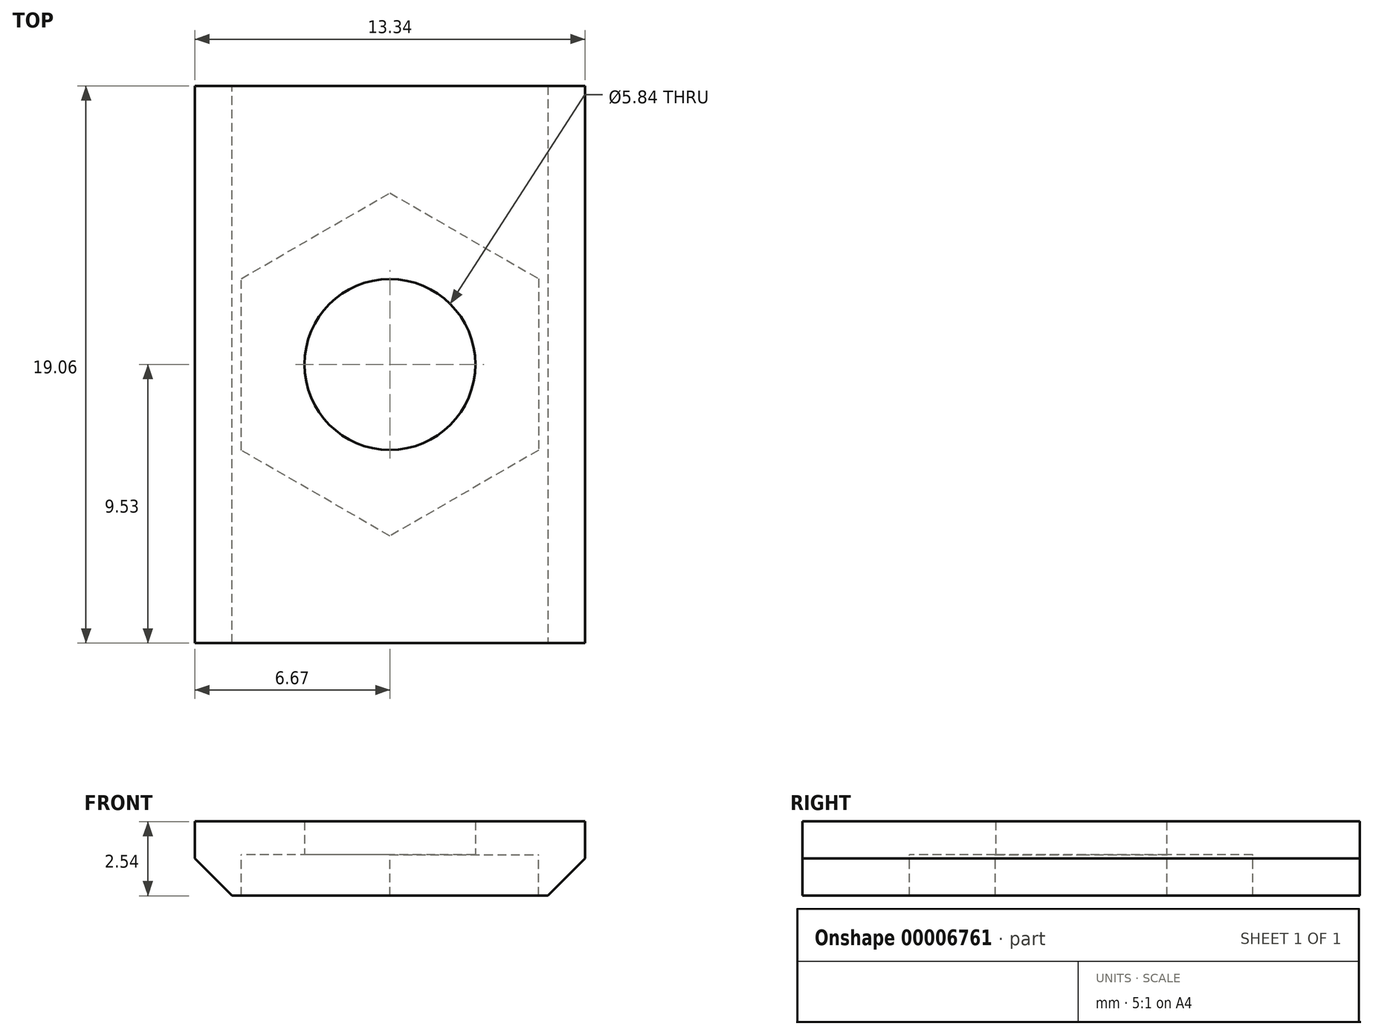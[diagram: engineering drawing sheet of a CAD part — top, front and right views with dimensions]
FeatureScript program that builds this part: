
annotation { "Feature Type Name" : "Feature", "Feature Type Description" : "" }
export const myFeature = defineFeature(function(context is Context, id is Id, definition is map)
    precondition{}
    {
        {
            var Q0;
            Q0=qCreatedBy(makeId("Top.planeOp"),FACE);
            var sketch = newSketch(context, id + "F0", { "sketchPlane" : qUnion([Q0])});
            skLineSegment(sketch, "E0.bottom", {"start": v(6.67, -9.53) * mm, "end": v(-6.67, -9.53) * mm});
            skLineSegment(sketch, "E0.top", {"start": v(6.67, 9.53) * mm, "end": v(-6.67, 9.53) * mm});
            skLineSegment(sketch, "E0.left", {"start": v(6.67, -9.53) * mm, "end": v(6.67, 9.53) * mm});
            skLineSegment(sketch, "E0.right", {"start": v(-6.67, -9.53) * mm, "end": v(-6.67, 9.53) * mm});
            skPoint(sketch, "E0.middle", {"position": v(0, 0) * mm});
            skCircle(sketch, "E1.cCircle", {"center": v(0, 0) * mm, "radius": 5.08 * mm, "construction": true});
            skLineSegment(sketch, "E1.0", {"start": v(5.08, -2.93) * mm, "end": v(0, -5.87) * mm});
            skLineSegment(sketch, "E1.1", {"start": v(0, -5.87) * mm, "end": v(-5.08, -2.93) * mm});
            skLineSegment(sketch, "E1.2", {"start": v(-5.08, -2.93) * mm, "end": v(-5.08, 2.93) * mm});
            skLineSegment(sketch, "E1.3", {"start": v(-5.08, 2.93) * mm, "end": v(0, 5.87) * mm});
            skLineSegment(sketch, "E1.4", {"start": v(0, 5.87) * mm, "end": v(5.08, 2.93) * mm});
            skLineSegment(sketch, "E1.5", {"start": v(5.08, 2.93) * mm, "end": v(5.08, -2.93) * mm});
            skPoint(sketch, "E1.0.midPoint", {"position": v(2.54, -4.4) * mm});
            skCircle(sketch, "E2", {"center": v(0, 0) * mm, "radius": 2.92 * mm});
            skSolve(sketch);
        }
        {
            var Q0;
            Q0=makeQuery(id+"F0.imprint","IMPRINT",FACE,{"disambiguationData":[TD([[makeQuery(id+"F0.imprint","IMPRINT",EDGE,{"derivedFrom":sQuery(id+"F0.wireOp",EDGE,"E0.bottom")}),-1.0]])]});
            var Q1;
            Q1=makeQuery(id+"F0.imprint","IMPRINT",FACE,{"disambiguationData":[TD([[makeQuery(id+"F0.imprint","IMPRINT",EDGE,{"derivedFrom":sQuery(id+"F0.wireOp",EDGE,"E1.0")}),-1.0]])]});
            extrude(context, id + "F1", {"entities" : qUnion([Q0, Q1]), "depth" : 1.14 * mm});
        }
        {
            var Q0;
            Q0=makeQuery(id+"F0.imprint","IMPRINT",FACE,{"disambiguationData":[TD([[makeQuery(id+"F0.imprint","IMPRINT",EDGE,{"derivedFrom":sQuery(id+"F0.wireOp",EDGE,"E0.bottom")}),-1.0]])]});
            extrude(context, id + "F2", {"entities" : qUnion([Q0]), "operationType" : NewBodyOperationType.ADD, "oppositeDirection" : true, "depth" : 1.4 * mm});
        }
        {
            var Q0;
            Q0=makeQuery(id+"F2.opExtrude","CAP_EDGE",EDGE,{"disambiguationData":[OSD([sQuery(id+"F0.wireOp",EDGE,"E0.left")])],"isStart":false});
            var Q1;
            Q1=makeQuery(id+"F2.opExtrude","CAP_EDGE",EDGE,{"disambiguationData":[OSD([sQuery(id+"F0.wireOp",EDGE,"E0.right")])],"isStart":false});
            chamfer(context, id + "F3", {"entities" : qUnion([Q0, Q1]), "width" : 1.27 * mm, "tangentPropagation" : true});
        }
    });
